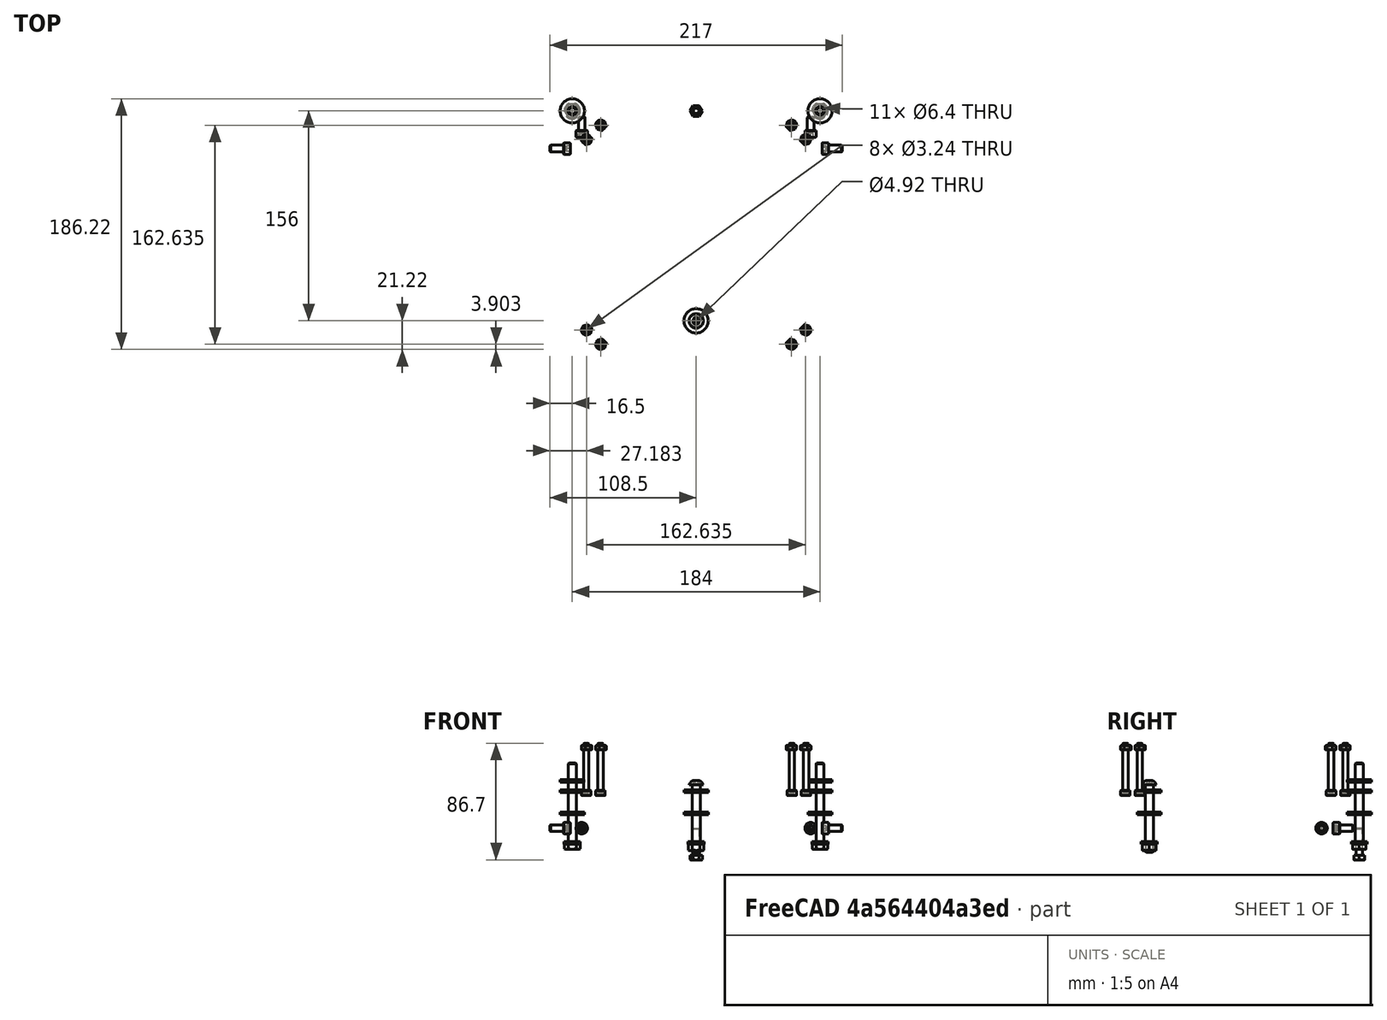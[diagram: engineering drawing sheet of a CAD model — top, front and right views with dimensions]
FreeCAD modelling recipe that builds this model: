
FCSTD DOCUMENT  (FreeCAD 0.19R24276 (Git))
Label: v5.6_Primary
License: All rights reserved
LicenseURL: http://en.wikipedia.org/wiki/All_rights_reserved
objects: App::Link×38, Part::FeaturePython×36, PartDesign::CoordinateSystem×7, App::DocumentObjectGroup×2, App::FeaturePython×1, App::Part×1
note: 43 computed .brp shape members not serialized (recipe doc carries the construction recipe); baked Part::Feature solids carry a one-line shape summary decoded from their .brp
EXTERNAL_REF file=v5.6_Master.FCStd obj=Local_CS
EXTERNAL_REF file=v5.6_Master.FCStd obj=Body014
EXTERNAL_REF file=v5.6_Master.FCStd obj=Local_CS001
EXTERNAL_REF file=v5.6_Master.FCStd obj=Local_CS005
EXTERNAL_REF file=v5.6_Master.FCStd obj=Body
EXTERNAL_REF file=v5.6_Master.FCStd obj=Local_CS002
EXTERNAL_REF file=v5.6_Master.FCStd obj=Local_CS006
EXTERNAL_REF file=v5.6_Master.FCStd obj=Body002
EXTERNAL_REF file=v5.6_Master.FCStd obj=Local_CS007
EXTERNAL_REF file=v5.6_Master.FCStd obj=Local_CS008
EXTERNAL_REF file=v5.6_Master.FCStd obj=LCS_LowerCell_Float_X
EXTERNAL_REF file=v5.6_Master.FCStd obj=Local_CS012
EXTERNAL_REF file=v5.6_Master.FCStd obj=Part
EXTERNAL_REF file=v5.6_Master.FCStd obj=LCS_LowerCell_RockerHole_P
EXTERNAL_REF file=v5.6_Master.FCStd obj=Local_CS024
EXTERNAL_REF file=v5.6_Master.FCStd obj=Body006
EXTERNAL_REF file=v5.6_Master.FCStd obj=LCS_LowerCell_RockerHole_S
EXTERNAL_REF file=v5.6_Master.FCStd obj=Local_CS028
EXTERNAL_REF file=v5.6_Master.FCStd obj=LCS_LowerCell_BCorner_AP
EXTERNAL_REF file=v5.6_Master.FCStd obj=Local_CS097
EXTERNAL_REF file=v5.6_Master.FCStd obj=Body038
EXTERNAL_REF file=v5.6_Master.FCStd obj=LCS_LowerCell_BCorner_AS
EXTERNAL_REF file=v5.6_Master.FCStd obj=LCS_LowerCell_CollPoint_F
EXTERNAL_REF file=v5.6_Master.FCStd obj=Local_CS191
EXTERNAL_REF file=v5.6_Master.FCStd obj=Body022010
EXTERNAL_REF file=v5.6_Master.FCStd obj=LCS_LowerCell_CollPoint_AP
EXTERNAL_REF file=v5.6_Master.FCStd obj=LCS_LowerCell_CollPoint_AS
EXTERNAL_REF file=v5.6_Master.FCStd obj=Local_CS081
EXTERNAL_REF file=v5.6_Master.FCStd obj=Local_CS086
EXTERNAL_REF file=v5.6_Master.FCStd obj=Body022
EXTERNAL_REF file=v5.6_Master.FCStd obj=Local_CS082
EXTERNAL_REF file=v5.6_Master.FCStd obj=Local_CS080
EXTERNAL_REF file=v5.6_Master.FCStd obj=Local_CS083
EXTERNAL_REF file=v5.6_Master.FCStd obj=Local_CS100
EXTERNAL_REF file=v5.6_Master.FCStd obj=Body039
EXTERNAL_REF file=v5.6_Master.FCStd obj=Local_CS026
EXTERNAL_REF file=v5.6_Master.FCStd obj=Local_CS030
EXTERNAL_REF file=v5.6_Master.FCStd obj=Local_CS108
EXTERNAL_REF file=v5.6_Master.FCStd obj=Local_CS109
EXTERNAL_REF file=v5.6_Master.FCStd obj=Local_CS009
EXTERNAL_REF file=v5.6_Master.FCStd obj=Local_CS114
EXTERNAL_REF file=v5.6_Master.FCStd obj=Local_CS115
EXTERNAL_REF file=v5.6_Master.FCStd obj=Local_CS116
EXTERNAL_REF file=v5.6_Master.FCStd obj=Local_CS117
EXTERNAL_REF file=v5.6_Master.FCStd obj=Local_CS118
EXTERNAL_REF file=v5.6_Master.FCStd obj=Local_CS119
EXTERNAL_REF file=v5.6_Master.FCStd obj=Local_CS120
EXTERNAL_REF file=v5.6_Master.FCStd obj=Local_CS121
EXTERNAL_REF file=v5.6_Master.FCStd obj=Local_CS098
EXTERNAL_REF file=v5.6_Master.FCStd obj=Local_CS099
EXTERNAL_REF file=v5.6_Master.FCStd obj=LCS_LowerCell_Pole_AP
EXTERNAL_REF file=v5.6_Master.FCStd obj=LCS_LowerCell_Pole_FP
EXTERNAL_REF file=v5.6_Master.FCStd obj=LCS_LowerCell_Pivot_X
EXTERNAL_REF file=v5.6_Master.FCStd obj=Local_CS039
EXTERNAL_REF file=v5.6_Master.FCStd obj=LCS_LowerCell_Pole_AS
EXTERNAL_REF file=v5.6_Master.FCStd obj=LCS_LowerCell_Pole_FS
EXTERNAL_REF file=v5.6_Master.FCStd obj=Local_CS011
EXTERNAL_REF file=v5.6_Master.FCStd obj=Local_CS010
EXTERNAL_REF file=v5.6_Master.FCStd obj=LCS_LowerCell_Counterweight
EXTERNAL_REF file=v5.6_Master.FCStd obj=Local_CS209
EXTERNAL_REF file=v5.6_Master.FCStd obj=Body022019
EXTERNAL_REF file=v5.6_Master.FCStd obj=Local_CS210
EXTERNAL_REF file=v5.6_Master.FCStd obj=Local_CS211
EXTERNAL_REF file=v5.6_Master.FCStd obj=Local_CS218
EXTERNAL_REF file=v5.6_Master.FCStd obj=Body017
EXTERNAL_REF file=v5.6_Master.FCStd obj=Local_CS087
EXTERNAL_REF file=v5.6_Master.FCStd obj=Local_CS088
EXTERNAL_REF file=v5.6_Master.FCStd obj=Local_CS235
EXTERNAL_REF file=v5.6_Master.FCStd obj=Body022032
EXTERNAL_REF file=v5.6_Master.FCStd obj=Local_CS234
EXTERNAL_REF file=v5.6_Master.FCStd obj=Body022030

FEATURE [App::DocumentObjectGroup] Parts
FEATURE [PartDesign::CoordinateSystem] LCS_Origin
  AttacherType = Attacher::AttachEngine3D
  MapMode = 2
  Support = -> [X_Axis]
FEATURE [App::DocumentObjectGroup] Constraints
FEATURE [App::FeaturePython] Variables  # WARN: FeaturePython — macro-defined, semantics opaque (R4)
FEATURE [App::Link] PrimaryMirror
  AssemblyType = Asm4EE
  AttachedBy = #Local_CS
  AttachedTo = Parent Assembly#LCS_Origin
  LinkedObject = -> <external v5.6_Master.FCStd>#Body014
  expr: Placement = LCS_Origin.Placement * AttachmentOffset * v5_6_Master#Local_CS.Placement ^ -1
FEATURE [App::Link] UpperCell
  AssemblyType = Asm4EE
  AttachedBy = #Local_CS005
  AttachedTo = PrimaryMirror#Local_CS001
  AttachmentOffset = pos=(0,0,0) rot=(0,0,1;1.5708rad)
  LinkPlacement = pos=(0,0,-37) rot=(0,0,1;0rad)
  LinkedObject = -> <external v5.6_Master.FCStd>#Body
  Placement = pos=(0,0,-37) rot=(0,0,1;0rad)
  expr: Placement = PrimaryMirror.Placement * v5_6_Master#Local_CS001.Placement * AttachmentOffset * v5_6_Master#Local_CS005.Placement ^ -1
FEATURE [App::Link] LowerPad_A
  AssemblyType = Asm4EE
  AttachedBy = #Local_CS002
  AttachedTo = UpperCell#Local_CS006
  LinkPlacement = pos=(0,60,-31) rot=(0,0,-1;1.5708rad)
  LinkedObject = -> <external v5.6_Master.FCStd>#Body002
  Placement = pos=(0,60,-31) rot=(0,0,-1;1.5708rad)
  expr: Placement = UpperCell.Placement * v5_6_Master#Local_CS006.Placement * AttachmentOffset * v5_6_Master#Local_CS002.Placement ^ -1
FEATURE [App::Link] LowerPad_FP
  AssemblyType = Asm4EE
  AttachedBy = #Local_CS002
  AttachedTo = UpperCell#Local_CS007
  LinkPlacement = pos=(51.9615,-30,-31) rot=(0,0,-1;3.66519rad)
  LinkedObject = -> <external v5.6_Master.FCStd>#Body002
  Placement = pos=(51.9615,-30,-31) rot=(0,0,-1;3.66519rad)
  expr: Placement = UpperCell.Placement * v5_6_Master#Local_CS007.Placement * AttachmentOffset * v5_6_Master#Local_CS002.Placement ^ -1
FEATURE [App::Link] LowerPad_FS
  AssemblyType = Asm4EE
  AttachedBy = #Local_CS002
  AttachedTo = UpperCell#Local_CS008
  LinkPlacement = pos=(-51.9615,-30,-31) rot=(0,0,1;0.523599rad)
  LinkedObject = -> <external v5.6_Master.FCStd>#Body002
  Placement = pos=(-51.9615,-30,-31) rot=(0,0,1;0.523599rad)
  expr: Placement = UpperCell.Placement * v5_6_Master#Local_CS008.Placement * AttachmentOffset * v5_6_Master#Local_CS002.Placement ^ -1
FEATURE [App::Link] LowerCell
  AssemblyType = Asm4EE
  AttachedBy = #LCS_LowerCell_Float_X
  AttachedTo = UpperCell#Local_CS012
  AttachmentOffset = pos=(0,0,0) rot=(0,0,1;4.71239rad)
  LinkPlacement = pos=(0,0,-65.2) rot=(0,0,1;0rad)
  LinkedObject = -> <external v5.6_Master.FCStd>#Part
  Placement = pos=(0,0,-65.2) rot=(0,0,1;0rad)
  expr: Placement = UpperCell.Placement * v5_6_Master#Local_CS012.Placement * AttachmentOffset * v5_6_Master#LCS_LowerCell_Float_X.Placement ^ -1
FEATURE [App::Link] Rocker_P
  AssemblyType = Asm4EE
  AttachedBy = #Local_CS024
  AttachedTo = LowerCell#LCS_LowerCell_RockerHole_P
  AttachmentOffset = pos=(0,0,0) rot=(0,1,0;3.14159rad)
  LinkPlacement = pos=(128,-7.11e-14,79.8) rot=(0,0,1;0rad)
  LinkedObject = -> <external v5.6_Master.FCStd>#Body006
  Placement = pos=(128,-7.11e-14,79.8) rot=(0,0,1;0rad)
  expr: Placement = LowerCell.Placement * v5_6_Master#LCS_LowerCell_RockerHole_P.Placement * AttachmentOffset * v5_6_Master#Local_CS024.Placement ^ -1
FEATURE [App::Link] Rocker_S
  AssemblyType = Asm4EE
  AttachedBy = #Local_CS028
  AttachedTo = LowerCell#LCS_LowerCell_RockerHole_S
  AttachmentOffset = pos=(0,0,0) rot=(1,0,0;3.14159rad)
  LinkPlacement = pos=(-128,5.68e-14,79.8) rot=(0,0,1;0rad)
  LinkedObject = -> <external v5.6_Master.FCStd>#Body006
  Placement = pos=(-128,5.68e-14,79.8) rot=(0,0,1;0rad)
  expr: Placement = LowerCell.Placement * v5_6_Master#LCS_LowerCell_RockerHole_S.Placement * AttachmentOffset * v5_6_Master#Local_CS028.Placement ^ -1
FEATURE [App::Link] LCFrame_Bracket_AP
  AssemblyType = Asm4EE
  AttachedBy = #Local_CS097
  AttachedTo = LowerCell#LCS_LowerCell_BCorner_AP
  AttachmentOffset = pos=(0,0,0) rot=(0,0,1;3.14159rad)
  LinkPlacement = pos=(103,82,-65.2) rot=(0,0,-1;3.14159rad)
  LinkedObject = -> <external v5.6_Master.FCStd>#Body038
  Placement = pos=(103,82,-65.2) rot=(0,0,-1;3.14159rad)
  expr: Placement = LowerCell.Placement * v5_6_Master#LCS_LowerCell_BCorner_AP.Placement * AttachmentOffset * v5_6_Master#Local_CS097.Placement ^ -1
FEATURE [App::Link] LCFrame_Bracket_AS
  AssemblyType = Asm4EE
  AttachedBy = #Local_CS097
  AttachedTo = LowerCell#LCS_LowerCell_BCorner_AS
  AttachmentOffset = pos=(0,0,0) rot=(0,0,1;4.71239rad)
  LinkPlacement = pos=(-103,82,-65.2) rot=(0,0,-1;1.5708rad)
  LinkedObject = -> <external v5.6_Master.FCStd>#Body038
  Placement = pos=(-103,82,-65.2) rot=(0,0,-1;1.5708rad)
  expr: Placement = LowerCell.Placement * v5_6_Master#LCS_LowerCell_BCorner_AS.Placement * AttachmentOffset * v5_6_Master#Local_CS097.Placement ^ -1
FEATURE [App::Link] CollSpring_F
  AssemblyType = Asm4EE
  AttachedBy = #Local_CS191
  AttachedTo = LowerCell#LCS_LowerCell_CollPoint_F
  AttachmentOffset = pos=(0,0,11.6) rot=(0,0,1;0rad)
  LinkPlacement = pos=(-2.84e-14,-64,-53.6) rot=(0,0,1;0rad)
  LinkedObject = -> <external v5.6_Master.FCStd>#Body022010
  Placement = pos=(-2.84e-14,-64,-53.6) rot=(0,0,1;0rad)
  expr: Placement = LowerCell.Placement * v5_6_Master#LCS_LowerCell_CollPoint_F.Placement * AttachmentOffset * v5_6_Master#Local_CS191.Placement ^ -1
FEATURE [App::Link] CollSpring_AP
  AssemblyType = Asm4EE
  AttachedBy = #Local_CS191
  AttachedTo = LowerCell#LCS_LowerCell_CollPoint_AP
  AttachmentOffset = pos=(0,0,11.6) rot=(0,0,1;0rad)
  LinkPlacement = pos=(92,92,-53.6) rot=(0,0,1;0rad)
  LinkedObject = -> <external v5.6_Master.FCStd>#Body022010
  Placement = pos=(92,92,-53.6) rot=(0,0,1;0rad)
  expr: Placement = LowerCell.Placement * v5_6_Master#LCS_LowerCell_CollPoint_AP.Placement * AttachmentOffset * v5_6_Master#Local_CS191.Placement ^ -1
FEATURE [App::Link] CollSpring_AS
  AssemblyType = Asm4EE
  AttachedBy = #Local_CS191
  AttachedTo = LowerCell#LCS_LowerCell_CollPoint_AS
  AttachmentOffset = pos=(0,0,11.6) rot=(0,0,1;0rad)
  LinkPlacement = pos=(-92,92,-53.6) rot=(0,0,1;0rad)
  LinkedObject = -> <external v5.6_Master.FCStd>#Body022010
  Placement = pos=(-92,92,-53.6) rot=(0,0,1;0rad)
  expr: Placement = LowerCell.Placement * v5_6_Master#LCS_LowerCell_CollPoint_AS.Placement * AttachmentOffset * v5_6_Master#Local_CS191.Placement ^ -1
FEATURE [App::Link] MirrorClip_AP
  AssemblyType = Asm4EE
  AttachedBy = #Local_CS086
  AttachedTo = UpperCell#Local_CS081
  LinkPlacement = pos=(72.4784,72.4784,-31) rot=(0,0,-1;0.785398rad)
  LinkedObject = -> <external v5.6_Master.FCStd>#Body022
  Placement = pos=(72.4784,72.4784,-31) rot=(0,0,-1;0.785398rad)
  expr: Placement = UpperCell.Placement * v5_6_Master#Local_CS081.Placement * AttachmentOffset * v5_6_Master#Local_CS086.Placement ^ -1
FEATURE [App::Link] MirrorClip_FP
  AssemblyType = Asm4EE
  AttachedBy = #Local_CS086
  AttachedTo = UpperCell#Local_CS082
  LinkPlacement = pos=(72.4784,-72.4784,-31) rot=(0,0,-1;2.35619rad)
  LinkedObject = -> <external v5.6_Master.FCStd>#Body022
  Placement = pos=(72.4784,-72.4784,-31) rot=(0,0,-1;2.35619rad)
  expr: Placement = UpperCell.Placement * v5_6_Master#Local_CS082.Placement * AttachmentOffset * v5_6_Master#Local_CS086.Placement ^ -1
FEATURE [App::Link] MirrorClip_AS
  AssemblyType = Asm4EE
  AttachedBy = #Local_CS086
  AttachedTo = UpperCell#Local_CS080
  LinkPlacement = pos=(-72.4784,72.4784,-31) rot=(0,0,-1;5.49779rad)
  LinkedObject = -> <external v5.6_Master.FCStd>#Body022
  Placement = pos=(-72.4784,72.4784,-31) rot=(0,0,-1;5.49779rad)
  expr: Placement = UpperCell.Placement * v5_6_Master#Local_CS080.Placement * AttachmentOffset * v5_6_Master#Local_CS086.Placement ^ -1
FEATURE [App::Link] MirrorClip_FS
  AssemblyType = Asm4EE
  AttachedBy = #Local_CS086
  AttachedTo = UpperCell#Local_CS083
  LinkPlacement = pos=(-72.4784,-72.4784,-31) rot=(0,0,-1;3.92699rad)
  LinkedObject = -> <external v5.6_Master.FCStd>#Body022
  Placement = pos=(-72.4784,-72.4784,-31) rot=(0,0,-1;3.92699rad)
  expr: Placement = UpperCell.Placement * v5_6_Master#Local_CS083.Placement * AttachmentOffset * v5_6_Master#Local_CS086.Placement ^ -1
FEATURE [App::Link] Rocker_P_TNut_A
  AssemblyType = Asm4EE
  AttachedBy = #Local_CS100
  AttachedTo = Rocker_P#Local_CS024
  AttachmentOffset = pos=(0,0,0) rot=(0.707107,-0.707107,0;3.14159rad)
  LinkPlacement = pos=(121.8,113,-65.2) rot=(-0.57735,0.57735,-0.57735;2.0944rad)
  LinkedObject = -> <external v5.6_Master.FCStd>#Body039
  Placement = pos=(121.8,113,-65.2) rot=(-0.57735,0.57735,-0.57735;2.0944rad)
  expr: Placement = Rocker_P.Placement * v5_6_Master#Local_CS024.Placement * AttachmentOffset * v5_6_Master#Local_CS100.Placement ^ -1
FEATURE [App::Link] Rocker_P_TNut_F
  AssemblyType = Asm4EE
  AttachedBy = #Local_CS100
  AttachedTo = Rocker_P#Local_CS026
  AttachmentOffset = pos=(0,0,0) rot=(0.707107,-0.707107,0;3.14159rad)
  LinkPlacement = pos=(121.8,-113,-65.2) rot=(-0.57735,0.57735,-0.57735;2.0944rad)
  LinkedObject = -> <external v5.6_Master.FCStd>#Body039
  Placement = pos=(121.8,-113,-65.2) rot=(-0.57735,0.57735,-0.57735;2.0944rad)
  expr: Placement = Rocker_P.Placement * v5_6_Master#Local_CS026.Placement * AttachmentOffset * v5_6_Master#Local_CS100.Placement ^ -1
FEATURE [App::Link] Rocker_S_TNut_A
  AssemblyType = Asm4EE
  AttachedBy = #Local_CS100
  AttachedTo = Rocker_S#Local_CS028
  AttachmentOffset = pos=(0,0,0) rot=(0.707107,-0.707107,0;3.14159rad)
  LinkPlacement = pos=(-121.8,113,-65.2) rot=(0.57735,-0.57735,-0.57735;2.0944rad)
  LinkedObject = -> <external v5.6_Master.FCStd>#Body039
  Placement = pos=(-121.8,113,-65.2) rot=(0.57735,-0.57735,-0.57735;2.0944rad)
  expr: Placement = Rocker_S.Placement * v5_6_Master#Local_CS028.Placement * AttachmentOffset * v5_6_Master#Local_CS100.Placement ^ -1
FEATURE [App::Link] Rocker_S_TNut_F
  AssemblyType = Asm4EE
  AttachedBy = #Local_CS100
  AttachedTo = Rocker_S#Local_CS030
  AttachmentOffset = pos=(0,0,0) rot=(0.707107,-0.707107,0;3.14159rad)
  LinkPlacement = pos=(-121.8,-113,-65.2) rot=(0.57735,-0.57735,-0.57735;2.0944rad)
  LinkedObject = -> <external v5.6_Master.FCStd>#Body039
  Placement = pos=(-121.8,-113,-65.2) rot=(0.57735,-0.57735,-0.57735;2.0944rad)
  expr: Placement = Rocker_S.Placement * v5_6_Master#Local_CS030.Placement * AttachmentOffset * v5_6_Master#Local_CS100.Placement ^ -1
FEATURE [App::Link] LCBracket_AP_TNut_P
  AssemblyType = Asm4EE
  AttachedBy = #Local_CS100
  AttachedTo = LCFrame_Bracket_AP#Local_CS108
  LinkPlacement = pos=(104.2,64,-65.2) rot=(0.57735,0.57735,-0.57735;4.18879rad)
  LinkedObject = -> <external v5.6_Master.FCStd>#Body039
  Placement = pos=(104.2,64,-65.2) rot=(0.57735,0.57735,-0.57735;4.18879rad)
  expr: Placement = LCFrame_Bracket_AP.Placement * v5_6_Master#Local_CS108.Placement * AttachmentOffset * v5_6_Master#Local_CS100.Placement ^ -1
FEATURE [App::Link] LCBracket_AP_TNut_A
  AssemblyType = Asm4EE
  AttachedBy = #Local_CS100
  AttachedTo = LCFrame_Bracket_AP#Local_CS109
  LinkPlacement = pos=(85,83.2,-65.2) rot=(0,0.707107,-0.707107;3.14159rad)
  LinkedObject = -> <external v5.6_Master.FCStd>#Body039
  Placement = pos=(85,83.2,-65.2) rot=(0,0.707107,-0.707107;3.14159rad)
  expr: Placement = LCFrame_Bracket_AP.Placement * v5_6_Master#Local_CS109.Placement * AttachmentOffset * v5_6_Master#Local_CS100.Placement ^ -1
FEATURE [App::Link] LCBracket_AS_TNut_S
  AssemblyType = Asm4EE
  AttachedBy = #Local_CS100
  AttachedTo = LCFrame_Bracket_AS#Local_CS109
  LinkPlacement = pos=(-104.2,64,-65.2) rot=(-0.57735,0.57735,-0.57735;2.0944rad)
  LinkedObject = -> <external v5.6_Master.FCStd>#Body039
  Placement = pos=(-104.2,64,-65.2) rot=(-0.57735,0.57735,-0.57735;2.0944rad)
  expr: Placement = LCFrame_Bracket_AS.Placement * v5_6_Master#Local_CS109.Placement * AttachmentOffset * v5_6_Master#Local_CS100.Placement ^ -1
FEATURE [App::Link] LCBracket_AS_TNut_A
  AssemblyType = Asm4EE
  AttachedBy = #Local_CS100
  AttachedTo = LCFrame_Bracket_AS#Local_CS108
  LinkPlacement = pos=(-85,83.2,-65.2) rot=(0,0.707107,-0.707107;3.14159rad)
  LinkedObject = -> <external v5.6_Master.FCStd>#Body039
  Placement = pos=(-85,83.2,-65.2) rot=(0,0.707107,-0.707107;3.14159rad)
  expr: Placement = LCFrame_Bracket_AS.Placement * v5_6_Master#Local_CS108.Placement * AttachmentOffset * v5_6_Master#Local_CS100.Placement ^ -1
FEATURE [Part::FeaturePython] Screw  label="M6x50-Screw"  # Fasteners workbench fastener (typed FeaturePython)
  AssemblyType = Asm4EE
  AttachedBy = Origin
  AttachedTo = UpperCell#Local_CS009
  Placement = pos=(0,-64,-33) rot=(0,0,1;0rad)
  diameter = 4
  invert = false
  length = 10
  lengthCustom = 50
  matchOuter = false
  offset = 0
  thread = false
  type = 38
  expr: Placement = UpperCell.Placement * v5_6_Master#Local_CS009.Placement * AttachmentOffset
FEATURE [Part::FeaturePython] Screw001  label="M6x60-Screw"  # Fasteners workbench fastener (typed FeaturePython)
  AssemblyType = Asm4EE
  AttachedBy = Origin
  AttachedTo = LowerCell#LCS_LowerCell_CollPoint_AP
  AttachmentOffset = pos=(0,0,-11.6) rot=(1,0,0;3.14159rad)
  Placement = pos=(92,92,-76.8) rot=(-1,0,0;3.14159rad)
  diameter = 8
  invert = false
  length = 11
  lengthCustom = 60
  matchOuter = false
  offset = 0
  thread = false
  type = 27
  expr: Placement = LowerCell.Placement * v5_6_Master#LCS_LowerCell_CollPoint_AP.Placement * AttachmentOffset
FEATURE [Part::FeaturePython] Screw002  label="M6x60-Screw001"  # Fasteners workbench fastener (typed FeaturePython)
  AssemblyType = Asm4EE
  AttachedBy = Origin
  AttachedTo = LowerCell#LCS_LowerCell_CollPoint_AS
  AttachmentOffset = pos=(0,0,-11.6) rot=(1,0,0;3.14159rad)
  Placement = pos=(-92,92,-76.8) rot=(-1,0,0;3.14159rad)
  diameter = 8
  invert = false
  length = 11
  lengthCustom = 60
  matchOuter = false
  offset = 0
  thread = false
  type = 27
  expr: Placement = LowerCell.Placement * v5_6_Master#LCS_LowerCell_CollPoint_AS.Placement * AttachmentOffset
FEATURE [Part::FeaturePython] Washer  label="M6-Washer"  # Fasteners workbench fastener (typed FeaturePython)
  AssemblyType = Asm4EE
  AttachedBy = Origin
  AttachedTo = LowerCell#LCS_LowerCell_CollPoint_F
  AttachmentOffset = pos=(0,0,10) rot=(0,0,1;0rad)
  Placement = pos=(-2.84e-14,-64,-55.2) rot=(0,0,1;0rad)
  diameter = 5
  invert = false
  matchOuter = false
  offset = 0
  type = 6
  expr: Placement = LowerCell.Placement * v5_6_Master#LCS_LowerCell_CollPoint_F.Placement * AttachmentOffset
FEATURE [Part::FeaturePython] Washer001  label="M6-Washer413"  # Fasteners workbench fastener (typed FeaturePython)
  AssemblyType = Asm4EE
  AttachedBy = Origin
  AttachedTo = LowerCell#LCS_LowerCell_CollPoint_F
  AttachmentOffset = pos=(0,0,26.6) rot=(0,0,1;0rad)
  Placement = pos=(-2.84e-14,-64,-38.6) rot=(0,0,1;0rad)
  diameter = 5
  invert = false
  matchOuter = false
  offset = 0
  type = 6
  expr: Placement = LowerCell.Placement * v5_6_Master#LCS_LowerCell_CollPoint_F.Placement * AttachmentOffset
FEATURE [Part::FeaturePython] Washer002  label="M6-Washer414"  # Fasteners workbench fastener (typed FeaturePython)
  AssemblyType = Asm4EE
  AttachedBy = Origin
  AttachedTo = LowerCell#LCS_LowerCell_CollPoint_AP
  AttachmentOffset = pos=(0,0,10) rot=(0,0,1;0rad)
  Placement = pos=(92,92,-55.2) rot=(0,0,1;0rad)
  diameter = 5
  invert = false
  matchOuter = false
  offset = 0
  type = 6
  expr: Placement = LowerCell.Placement * v5_6_Master#LCS_LowerCell_CollPoint_AP.Placement * AttachmentOffset
FEATURE [Part::FeaturePython] Washer003  label="M6-Washer415"  # Fasteners workbench fastener (typed FeaturePython)
  AssemblyType = Asm4EE
  AttachedBy = Origin
  AttachedTo = LowerCell#LCS_LowerCell_CollPoint_AP
  AttachmentOffset = pos=(0,0,26.6) rot=(0,0,1;0rad)
  Placement = pos=(92,92,-38.6) rot=(0,0,1;0rad)
  diameter = 5
  invert = false
  matchOuter = false
  offset = 0
  type = 6
  expr: Placement = LowerCell.Placement * v5_6_Master#LCS_LowerCell_CollPoint_AP.Placement * AttachmentOffset
FEATURE [Part::FeaturePython] Washer004  label="M6-Washer416"  # Fasteners workbench fastener (typed FeaturePython)
  AssemblyType = Asm4EE
  AttachedBy = Origin
  AttachedTo = LowerCell#LCS_LowerCell_CollPoint_AS
  AttachmentOffset = pos=(0,0,10) rot=(0,0,1;0rad)
  Placement = pos=(-92,92,-55.2) rot=(0,0,1;0rad)
  diameter = 5
  invert = false
  matchOuter = false
  offset = 0
  type = 6
  expr: Placement = LowerCell.Placement * v5_6_Master#LCS_LowerCell_CollPoint_AS.Placement * AttachmentOffset
FEATURE [Part::FeaturePython] Washer005  label="M6-Washer417"  # Fasteners workbench fastener (typed FeaturePython)
  AssemblyType = Asm4EE
  AttachedBy = Origin
  AttachedTo = LowerCell#LCS_LowerCell_CollPoint_AS
  AttachmentOffset = pos=(0,0,26.6) rot=(0,0,1;0rad)
  Placement = pos=(-92,92,-38.6) rot=(0,0,1;0rad)
  diameter = 5
  invert = false
  matchOuter = false
  offset = 0
  type = 6
  expr: Placement = LowerCell.Placement * v5_6_Master#LCS_LowerCell_CollPoint_AS.Placement * AttachmentOffset
FEATURE [Part::FeaturePython] Screw003  label="M4x35-Screw"  # Fasteners workbench fastener (typed FeaturePython)
  AssemblyType = Asm4EE
  AttachedBy = Origin
  AttachedTo = UpperCell#Local_CS114
  Placement = pos=(-81.6708,-71.0642,-37) rot=(0.382683,0.92388,0;3.14159rad)
  diameter = 5
  invert = false
  length = 9
  lengthCustom = 35
  matchOuter = false
  offset = 0
  thread = false
  type = 32
  expr: Placement = UpperCell.Placement * v5_6_Master#Local_CS114.Placement * AttachmentOffset
FEATURE [Part::FeaturePython] Screw004  label="M4x35-Screw211"  # Fasteners workbench fastener (typed FeaturePython)
  AssemblyType = Asm4EE
  AttachedBy = Origin
  AttachedTo = UpperCell#Local_CS115
  Placement = pos=(-71.0642,-81.6708,-37) rot=(0.382683,0.92388,0;3.14159rad)
  diameter = 5
  invert = false
  length = 9
  lengthCustom = 35
  matchOuter = false
  offset = 0
  thread = false
  type = 32
  expr: Placement = UpperCell.Placement * v5_6_Master#Local_CS115.Placement * AttachmentOffset
FEATURE [Part::FeaturePython] Screw005  label="M4x35-Screw212"  # Fasteners workbench fastener (typed FeaturePython)
  AssemblyType = Asm4EE
  AttachedBy = Origin
  AttachedTo = UpperCell#Local_CS116
  Placement = pos=(71.0642,-81.6708,-37) rot=(-0.382683,0.92388,0;3.14159rad)
  diameter = 5
  invert = false
  length = 9
  lengthCustom = 35
  matchOuter = false
  offset = 0
  thread = false
  type = 32
  expr: Placement = UpperCell.Placement * v5_6_Master#Local_CS116.Placement * AttachmentOffset
FEATURE [Part::FeaturePython] Screw006  label="M4x35-Screw213"  # Fasteners workbench fastener (typed FeaturePython)
  AssemblyType = Asm4EE
  AttachedBy = Origin
  AttachedTo = UpperCell#Local_CS117
  Placement = pos=(81.6708,-71.0642,-37) rot=(-0.382683,0.92388,0;3.14159rad)
  diameter = 5
  invert = false
  length = 9
  lengthCustom = 35
  matchOuter = false
  offset = 0
  thread = false
  type = 32
  expr: Placement = UpperCell.Placement * v5_6_Master#Local_CS117.Placement * AttachmentOffset
FEATURE [Part::FeaturePython] Screw007  label="M4x35-Screw214"  # Fasteners workbench fastener (typed FeaturePython)
  AssemblyType = Asm4EE
  AttachedBy = Origin
  AttachedTo = UpperCell#Local_CS118
  Placement = pos=(-81.6708,71.0642,-37) rot=(0.92388,0.382683,0;3.14159rad)
  diameter = 5
  invert = false
  length = 9
  lengthCustom = 35
  matchOuter = false
  offset = 0
  thread = false
  type = 32
  expr: Placement = UpperCell.Placement * v5_6_Master#Local_CS118.Placement * AttachmentOffset
FEATURE [Part::FeaturePython] Screw008  label="M4x35-Screw215"  # Fasteners workbench fastener (typed FeaturePython)
  AssemblyType = Asm4EE
  AttachedBy = Origin
  AttachedTo = UpperCell#Local_CS119
  Placement = pos=(-71.0642,81.6708,-37) rot=(0.92388,0.382683,0;3.14159rad)
  diameter = 5
  invert = false
  length = 9
  lengthCustom = 35
  matchOuter = false
  offset = 0
  thread = false
  type = 32
  expr: Placement = UpperCell.Placement * v5_6_Master#Local_CS119.Placement * AttachmentOffset
FEATURE [Part::FeaturePython] Screw009  label="M4x35-Screw216"  # Fasteners workbench fastener (typed FeaturePython)
  AssemblyType = Asm4EE
  AttachedBy = Origin
  AttachedTo = UpperCell#Local_CS120
  Placement = pos=(81.6708,71.0642,-37) rot=(0.92388,-0.382683,0;3.14159rad)
  diameter = 5
  invert = false
  length = 9
  lengthCustom = 35
  matchOuter = false
  offset = 0
  thread = false
  type = 32
  expr: Placement = UpperCell.Placement * v5_6_Master#Local_CS120.Placement * AttachmentOffset
FEATURE [Part::FeaturePython] Screw010  label="M4x35-Screw217"  # Fasteners workbench fastener (typed FeaturePython)
  AssemblyType = Asm4EE
  AttachedBy = Origin
  AttachedTo = UpperCell#Local_CS121
  Placement = pos=(71.0642,81.6708,-37) rot=(0.92388,-0.382683,0;3.14159rad)
  diameter = 5
  invert = false
  length = 9
  lengthCustom = 35
  matchOuter = false
  offset = 0
  thread = false
  type = 32
  expr: Placement = UpperCell.Placement * v5_6_Master#Local_CS121.Placement * AttachmentOffset
FEATURE [Part::FeaturePython] Screw011  label="M5x10-Screw"  # Fasteners workbench fastener (typed FeaturePython)
  AssemblyType = Asm4EE
  AttachedBy = Origin
  AttachedTo = LCFrame_Bracket_AP#Local_CS098
  Placement = pos=(98.5,64,-65.2) rot=(0.57735,-0.57735,-0.57735;2.0944rad)
  diameter = 6
  invert = false
  length = 1
  lengthCustom = 10
  matchOuter = false
  offset = 0
  thread = false
  type = 32
  expr: Placement = LCFrame_Bracket_AP.Placement * v5_6_Master#Local_CS098.Placement * AttachmentOffset
FEATURE [Part::FeaturePython] Screw012  label="M5x10-Screw133"  # Fasteners workbench fastener (typed FeaturePython)
  AssemblyType = Asm4EE
  AttachedBy = Origin
  AttachedTo = LCFrame_Bracket_AP#Local_CS099
  Placement = pos=(85,77.5,-65.2) rot=(0.57735,0.57735,-0.57735;2.0944rad)
  diameter = 6
  invert = false
  length = 1
  lengthCustom = 10
  matchOuter = false
  offset = 0
  thread = false
  type = 32
  expr: Placement = LCFrame_Bracket_AP.Placement * v5_6_Master#Local_CS099.Placement * AttachmentOffset
FEATURE [Part::FeaturePython] Screw013  label="M5x10-Screw134"  # Fasteners workbench fastener (typed FeaturePython)
  AssemblyType = Asm4EE
  AttachedBy = Origin
  AttachedTo = LCFrame_Bracket_AS#Local_CS098
  Placement = pos=(-85,77.5,-65.2) rot=(1,0,0;1.5708rad)
  diameter = 6
  invert = false
  length = 1
  lengthCustom = 10
  matchOuter = false
  offset = 0
  thread = false
  type = 32
  expr: Placement = LCFrame_Bracket_AS.Placement * v5_6_Master#Local_CS098.Placement * AttachmentOffset
FEATURE [Part::FeaturePython] Screw014  label="M5x10-Screw135"  # Fasteners workbench fastener (typed FeaturePython)
  AssemblyType = Asm4EE
  AttachedBy = Origin
  AttachedTo = LCFrame_Bracket_AS#Local_CS099
  Placement = pos=(-98.5,64,-65.2) rot=(0,1,0;1.5708rad)
  diameter = 6
  invert = false
  length = 1
  lengthCustom = 10
  matchOuter = false
  offset = 0
  thread = false
  type = 32
  expr: Placement = LCFrame_Bracket_AS.Placement * v5_6_Master#Local_CS099.Placement * AttachmentOffset
FEATURE [App::Link] PoleBase_TNut_A
  AssemblyType = Asm4EE
  AttachedBy = #Local_CS100
  AttachedTo = LowerCell#LCS_LowerCell_Pole_AP
  AttachmentOffset = pos=(0,0,0) rot=(0,0,1;1.5708rad)
  LinkPlacement = pos=(113,113,-56.4) rot=(0,0,1;4.71239rad)
  LinkedObject = -> <external v5.6_Master.FCStd>#Body039
  Placement = pos=(113,113,-56.4) rot=(0,0,1;4.71239rad)
  expr: Placement = LowerCell.Placement * v5_6_Master#LCS_LowerCell_Pole_AP.Placement * AttachmentOffset * v5_6_Master#Local_CS100.Placement ^ -1
FEATURE [App::Link] PoleBase_TNut_F
  AssemblyType = Asm4EE
  AttachedBy = #Local_CS100
  AttachedTo = LowerCell#LCS_LowerCell_Pole_FP
  AttachmentOffset = pos=(0,0,0) rot=(0,0,1;1.5708rad)
  LinkPlacement = pos=(113,-113,-56.4) rot=(0,0,1;4.71239rad)
  LinkedObject = -> <external v5.6_Master.FCStd>#Body039
  Placement = pos=(113,-113,-56.4) rot=(0,0,1;4.71239rad)
  expr: Placement = LowerCell.Placement * v5_6_Master#LCS_LowerCell_Pole_FP.Placement * AttachmentOffset * v5_6_Master#Local_CS100.Placement ^ -1
FEATURE [PartDesign::CoordinateSystem] LCS_Pivot
  AttacherType = Attacher::AttachEngine3D
  Placement = pos=(0,0,79.8) rot=(0,0,1;0rad)
  expr: Placement = LowerCell.Placement * v5_6_Master#LCS_LowerCell_Pivot_X.Placement * AttachmentOffset
FEATURE [PartDesign::CoordinateSystem] LCS_SecondaryAssembly
  AttacherType = Attacher::AttachEngine3D
  Placement = pos=(0,0,834) rot=(0,0,1;0rad)
  expr: Placement = PrimaryMirror.Placement * v5_6_Master#Local_CS039.Placement * AttachmentOffset
FEATURE [PartDesign::CoordinateSystem] LCS_Primary_Pole_AP
  AttacherType = Attacher::AttachEngine3D
  Placement = pos=(113,113,-55.2) rot=(0,0,1;0rad)
  expr: Placement = LowerCell.Placement * v5_6_Master#LCS_LowerCell_Pole_AP.Placement * AttachmentOffset
FEATURE [PartDesign::CoordinateSystem] LCS_Primary_Pole_AS
  AttacherType = Attacher::AttachEngine3D
  Placement = pos=(-113,113,-65.2) rot=(0,0,1;0rad)
  expr: Placement = LowerCell.Placement * v5_6_Master#LCS_LowerCell_Pole_AS.Placement * AttachmentOffset
FEATURE [PartDesign::CoordinateSystem] LCS_Primary_Pole_FP
  AttacherType = Attacher::AttachEngine3D
  Placement = pos=(113,-113,-55.2) rot=(0,0,1;0rad)
  expr: Placement = LowerCell.Placement * v5_6_Master#LCS_LowerCell_Pole_FP.Placement * AttachmentOffset
FEATURE [PartDesign::CoordinateSystem] LCS_Primary_Pole_FS
  AttacherType = Attacher::AttachEngine3D
  Placement = pos=(-113,-113,-55.2) rot=(0,0,1;0rad)
  expr: Placement = LowerCell.Placement * v5_6_Master#LCS_LowerCell_Pole_FS.Placement * AttachmentOffset
FEATURE [Part::FeaturePython] Washer006  label="M6-Washer418"  # Fasteners workbench fastener (typed FeaturePython)
  AssemblyType = Asm4EE
  AttachedBy = Origin
  AttachedTo = LowerCell#LCS_LowerCell_CollPoint_F
  AttachmentOffset = pos=(0,0,-10) rot=(1,0,0;3.14159rad)
  Placement = pos=(-2.84e-14,-64,-75.2) rot=(-1,0,0;3.14159rad)
  diameter = 7
  invert = false
  matchOuter = false
  offset = 0
  type = 3
  expr: Placement = LowerCell.Placement * v5_6_Master#LCS_LowerCell_CollPoint_F.Placement * AttachmentOffset
FEATURE [Part::FeaturePython] Nut  label="M6-Nut"  # Fasteners workbench fastener (typed FeaturePython)
  AssemblyType = Asm4EE
  AttachedBy = Origin
  AttachedTo = LowerCell#LCS_LowerCell_CollPoint_F
  AttachmentOffset = pos=(0,0,-11.8) rot=(1,0,0;3.14159rad)
  Placement = pos=(-2.84e-14,-64,-77) rot=(-1,0,0;3.14159rad)
  diameter = 8
  invert = false
  matchOuter = false
  offset = 0
  thread = false
  type = 7
  expr: Placement = LowerCell.Placement * v5_6_Master#LCS_LowerCell_CollPoint_F.Placement * AttachmentOffset
FEATURE [Part::FeaturePython] Washer007  label="M6-Washer419"  # Fasteners workbench fastener (typed FeaturePython)
  AssemblyType = Asm4EE
  AttachedBy = Origin
  AttachedTo = UpperCell#Local_CS011
  Placement = pos=(92,92,-31) rot=(0,0,1;0rad)
  diameter = 5
  invert = false
  matchOuter = false
  offset = 0
  type = 6
  expr: Placement = UpperCell.Placement * v5_6_Master#Local_CS011.Placement * AttachmentOffset
FEATURE [Part::FeaturePython] Washer008  label="M6-Washer420"  # Fasteners workbench fastener (typed FeaturePython)
  AssemblyType = Asm4EE
  AttachedBy = Origin
  AttachedTo = UpperCell#Local_CS010
  Placement = pos=(-92,92,-31) rot=(0,0,1;0rad)
  diameter = 5
  invert = false
  matchOuter = false
  offset = 0
  type = 6
  expr: Placement = UpperCell.Placement * v5_6_Master#Local_CS010.Placement * AttachmentOffset
FEATURE [Part::FeaturePython] Washer009  label="M6-Washer421"  # Fasteners workbench fastener (typed FeaturePython)
  AssemblyType = Asm4EE
  AttachedBy = Origin
  AttachedTo = LowerCell#LCS_LowerCell_CollPoint_AP
  AttachmentOffset = pos=(0,0,-10) rot=(1,0,0;3.14159rad)
  Placement = pos=(92,92,-75.2) rot=(-1,0,0;3.14159rad)
  diameter = 7
  invert = false
  matchOuter = false
  offset = 0
  type = 3
  expr: Placement = LowerCell.Placement * v5_6_Master#LCS_LowerCell_CollPoint_AP.Placement * AttachmentOffset
FEATURE [Part::FeaturePython] Washer010  label="M6-Washer422"  # Fasteners workbench fastener (typed FeaturePython)
  AssemblyType = Asm4EE
  AttachedBy = Origin
  AttachedTo = LowerCell#LCS_LowerCell_CollPoint_AS
  AttachmentOffset = pos=(0,0,-10) rot=(1,0,0;3.14159rad)
  Placement = pos=(-92,92,-75.2) rot=(-1,0,0;3.14159rad)
  diameter = 7
  invert = false
  matchOuter = false
  offset = 0
  type = 3
  expr: Placement = LowerCell.Placement * v5_6_Master#LCS_LowerCell_CollPoint_AS.Placement * AttachmentOffset
FEATURE [App::Link] CounterWeightClamp
  AssemblyType = Asm4EE
  AttachedBy = #Local_CS209
  AttachedTo = LowerCell#LCS_LowerCell_Counterweight
  AttachmentOffset = pos=(0,0,0) rot=(1,0,0;3.14159rad)
  LinkPlacement = pos=(4.09e-14,92,-75.2) rot=(0,0,1;0rad)
  LinkedObject = -> <external v5.6_Master.FCStd>#Body022019
  Placement = pos=(4.09e-14,92,-75.2) rot=(0,0,1;0rad)
  expr: Placement = LowerCell.Placement * v5_6_Master#LCS_LowerCell_Counterweight.Placement * AttachmentOffset * v5_6_Master#Local_CS209.Placement ^ -1
FEATURE [App::Link] CW_TNut
  AssemblyType = Asm4EE
  AttachedBy = #Local_CS100
  AttachedTo = CounterWeightClamp#Local_CS209
  LinkPlacement = pos=(4.09e-14,92,-74) rot=(0,-1,0;3.14159rad)
  LinkedObject = -> <external v5.6_Master.FCStd>#Body039
  Placement = pos=(4.09e-14,92,-74) rot=(0,-1,0;3.14159rad)
  expr: Placement = CounterWeightClamp.Placement * v5_6_Master#Local_CS209.Placement * AttachmentOffset * v5_6_Master#Local_CS100.Placement ^ -1
FEATURE [Part::FeaturePython] Screw026  label="M5x20-Screw"  # Fasteners workbench fastener (typed FeaturePython)
  AssemblyType = Asm4EE
  AttachedBy = Origin
  AttachedTo = CounterWeightClamp#Local_CS210
  AttachmentOffset = pos=(0,0,0) rot=(1,0,0;3.14159rad)
  Placement = pos=(4.75e-14,92,-85.2) rot=(0,-1,0;3.14159rad)
  diameter = 7
  invert = false
  length = 5
  lengthCustom = 20
  matchOuter = false
  offset = 0
  thread = false
  type = 27
  expr: Placement = CounterWeightClamp.Placement * v5_6_Master#Local_CS210.Placement * AttachmentOffset
FEATURE [App::Link] CounterWeight
  AssemblyType = Asm4EE
  AttachedBy = #Local_CS218
  AttachedTo = CounterWeightClamp#Local_CS211
  LinkPlacement = pos=(4.09e-14,92,-95.2) rot=(0,0,-1;4.71239rad)
  LinkedObject = -> <external v5.6_Master.FCStd>#Body017
  Placement = pos=(4.09e-14,92,-95.2) rot=(0,0,-1;4.71239rad)
  expr: Placement = CounterWeightClamp.Placement * v5_6_Master#Local_CS211.Placement * AttachmentOffset * v5_6_Master#Local_CS218.Placement ^ -1
FEATURE [Part::FeaturePython] Nut001  label="M4-Nut"  # Fasteners workbench fastener (typed FeaturePython)
  AssemblyType = Asm4EE
  AttachedBy = Origin
  AttachedTo = MirrorClip_AP#Local_CS087
  AttachmentOffset = pos=(0,0,24) rot=(0,0,1;1.5708rad)
  Placement = pos=(81.3173,70.7107,-7) rot=(0,0,1;2.35619rad)
  diameter = 6
  invert = false
  matchOuter = false
  offset = 0
  thread = false
  type = 7
  expr: Placement = MirrorClip_AP.Placement * v5_6_Master#Local_CS087.Placement * AttachmentOffset
FEATURE [Part::FeaturePython] Nut002  label="M4-Nut079"  # Fasteners workbench fastener (typed FeaturePython)
  AssemblyType = Asm4EE
  AttachedBy = Origin
  AttachedTo = MirrorClip_AP#Local_CS088
  AttachmentOffset = pos=(0,0,24) rot=(0,0,1;1.5708rad)
  Placement = pos=(70.7107,81.3173,-7) rot=(0,0,1;2.35619rad)
  diameter = 6
  invert = false
  matchOuter = false
  offset = 0
  thread = false
  type = 7
  expr: Placement = MirrorClip_AP.Placement * v5_6_Master#Local_CS088.Placement * AttachmentOffset
FEATURE [Part::FeaturePython] Nut003  label="M4-Nut080"  # Fasteners workbench fastener (typed FeaturePython)
  AssemblyType = Asm4EE
  AttachedBy = Origin
  AttachedTo = MirrorClip_FP#Local_CS087
  AttachmentOffset = pos=(0,0,24) rot=(0,0,1;1.5708rad)
  Placement = pos=(70.7107,-81.3173,-7) rot=(0,0,1;0.785398rad)
  diameter = 6
  invert = false
  matchOuter = false
  offset = 0
  thread = false
  type = 7
  expr: Placement = MirrorClip_FP.Placement * v5_6_Master#Local_CS087.Placement * AttachmentOffset
FEATURE [Part::FeaturePython] Nut004  label="M4-Nut081"  # Fasteners workbench fastener (typed FeaturePython)
  AssemblyType = Asm4EE
  AttachedBy = Origin
  AttachedTo = MirrorClip_FP#Local_CS088
  AttachmentOffset = pos=(0,0,24) rot=(0,0,1;1.5708rad)
  Placement = pos=(81.3173,-70.7107,-7) rot=(0,0,1;0.785398rad)
  diameter = 6
  invert = false
  matchOuter = false
  offset = 0
  thread = false
  type = 7
  expr: Placement = MirrorClip_FP.Placement * v5_6_Master#Local_CS088.Placement * AttachmentOffset
FEATURE [Part::FeaturePython] Nut005  label="M4-Nut082"  # Fasteners workbench fastener (typed FeaturePython)
  AssemblyType = Asm4EE
  AttachedBy = Origin
  AttachedTo = MirrorClip_AS#Local_CS087
  AttachmentOffset = pos=(0,0,24) rot=(0,0,1;1.5708rad)
  Placement = pos=(-70.7107,81.3173,-7) rot=(0,0,-1;2.35619rad)
  diameter = 6
  invert = false
  matchOuter = false
  offset = 0
  thread = false
  type = 7
  expr: Placement = MirrorClip_AS.Placement * v5_6_Master#Local_CS087.Placement * AttachmentOffset
FEATURE [Part::FeaturePython] Nut006  label="M4-Nut083"  # Fasteners workbench fastener (typed FeaturePython)
  AssemblyType = Asm4EE
  AttachedBy = Origin
  AttachedTo = MirrorClip_AS#Local_CS088
  AttachmentOffset = pos=(0,0,24) rot=(0,0,1;0rad)
  Placement = pos=(-81.3173,70.7107,-7) rot=(0,0,-1;3.92699rad)
  diameter = 6
  invert = false
  matchOuter = false
  offset = 0
  thread = false
  type = 7
  expr: Placement = MirrorClip_AS.Placement * v5_6_Master#Local_CS088.Placement * AttachmentOffset
FEATURE [Part::FeaturePython] Nut007  label="M4-Nut084"  # Fasteners workbench fastener (typed FeaturePython)
  AssemblyType = Asm4EE
  AttachedBy = Origin
  AttachedTo = MirrorClip_FS#Local_CS087
  AttachmentOffset = pos=(0,0,24) rot=(0,0,1;1.5708rad)
  Placement = pos=(-81.3173,-70.7107,-7) rot=(0,0,-1;0.785398rad)
  diameter = 6
  invert = false
  matchOuter = false
  offset = 0
  thread = false
  type = 7
  expr: Placement = MirrorClip_FS.Placement * v5_6_Master#Local_CS087.Placement * AttachmentOffset
FEATURE [Part::FeaturePython] Nut008  label="M4-Nut085"  # Fasteners workbench fastener (typed FeaturePython)
  AssemblyType = Asm4EE
  AttachedBy = Origin
  AttachedTo = MirrorClip_FS#Local_CS088
  AttachmentOffset = pos=(0,0,24) rot=(0,0,1;1.5708rad)
  Placement = pos=(-70.7107,-81.3173,-7) rot=(0,0,-1;0.785398rad)
  diameter = 6
  invert = false
  matchOuter = false
  offset = 0
  thread = false
  type = 7
  expr: Placement = MirrorClip_FS.Placement * v5_6_Master#Local_CS088.Placement * AttachmentOffset
FEATURE [App::Link] RockerKnob_AP
  AssemblyType = Asm4EE
  AttachedBy = #Local_CS235
  AttachedTo = Rocker_P#Local_CS028
  LinkPlacement = pos=(133,113,-65.2) rot=(-0.57735,-0.57735,-0.57735;4.18879rad)
  LinkedObject = -> <external v5.6_Master.FCStd>#Body022032
  Placement = pos=(133,113,-65.2) rot=(-0.57735,-0.57735,-0.57735;4.18879rad)
  expr: Placement = Rocker_P.Placement * v5_6_Master#Local_CS028.Placement * AttachmentOffset * v5_6_Master#Local_CS235.Placement ^ -1
FEATURE [App::Link] RockerKnob_FP
  AssemblyType = Asm4EE
  AttachedBy = #Local_CS235
  AttachedTo = Rocker_P#Local_CS030
  LinkPlacement = pos=(133,-113,-65.2) rot=(-0.57735,-0.57735,-0.57735;4.18879rad)
  LinkedObject = -> <external v5.6_Master.FCStd>#Body022032
  Placement = pos=(133,-113,-65.2) rot=(-0.57735,-0.57735,-0.57735;4.18879rad)
  expr: Placement = Rocker_P.Placement * v5_6_Master#Local_CS030.Placement * AttachmentOffset * v5_6_Master#Local_CS235.Placement ^ -1
FEATURE [App::Link] RockerKnob_AS
  AssemblyType = Asm4EE
  AttachedBy = #Local_CS235
  AttachedTo = Rocker_S#Local_CS024
  LinkPlacement = pos=(-133,113,-65.2) rot=(-0.57735,-0.57735,0.57735;2.0944rad)
  LinkedObject = -> <external v5.6_Master.FCStd>#Body022032
  Placement = pos=(-133,113,-65.2) rot=(-0.57735,-0.57735,0.57735;2.0944rad)
  expr: Placement = Rocker_S.Placement * v5_6_Master#Local_CS024.Placement * AttachmentOffset * v5_6_Master#Local_CS235.Placement ^ -1
FEATURE [App::Link] RockerKnob_FS
  AssemblyType = Asm4EE
  AttachedBy = #Local_CS235
  AttachedTo = Rocker_S#Local_CS026
  LinkPlacement = pos=(-133,-113,-65.2) rot=(-0.57735,-0.57735,0.57735;2.0944rad)
  LinkedObject = -> <external v5.6_Master.FCStd>#Body022032
  Placement = pos=(-133,-113,-65.2) rot=(-0.57735,-0.57735,0.57735;2.0944rad)
  expr: Placement = Rocker_S.Placement * v5_6_Master#Local_CS026.Placement * AttachmentOffset * v5_6_Master#Local_CS235.Placement ^ -1
FEATURE [App::Link] CollKnob_AP001  label="CollKnob_AP"
  AssemblyType = Asm4EE
  AttachedBy = #Local_CS234
  AttachedTo = UpperCell#Local_CS011
  AttachmentOffset = pos=(0,0,1.6) rot=(0,0,1;0rad)
  LinkPlacement = pos=(92,92,-29.4) rot=(0,0,-1;1.5708rad)
  LinkedObject = -> <external v5.6_Master.FCStd>#Body022030
  Placement = pos=(92,92,-29.4) rot=(0,0,-1;1.5708rad)
  expr: Placement = UpperCell.Placement * v5_6_Master#Local_CS011.Placement * AttachmentOffset * v5_6_Master#Local_CS234.Placement ^ -1
FEATURE [App::Link] CollKnob_AS001  label="CollKnob_AS"
  AssemblyType = Asm4EE
  AttachedBy = #Local_CS234
  AttachedTo = UpperCell#Local_CS010
  AttachmentOffset = pos=(0,0,1.6) rot=(0,0,1;0rad)
  LinkPlacement = pos=(-92,92,-29.4) rot=(0,0,-1;1.5708rad)
  LinkedObject = -> <external v5.6_Master.FCStd>#Body022030
  Placement = pos=(-92,92,-29.4) rot=(0,0,-1;1.5708rad)
  expr: Placement = UpperCell.Placement * v5_6_Master#Local_CS010.Placement * AttachmentOffset * v5_6_Master#Local_CS234.Placement ^ -1
FEATURE [App::Link] PoleBase_TNut_AS
  AssemblyType = Asm4EE
  AttachedBy = #Local_CS100
  AttachedTo = LowerCell#LCS_LowerCell_Pole_AS
  AttachmentOffset = pos=(0,0,10) rot=(0,0,1;1.5708rad)
  LinkPlacement = pos=(-113,113,-56.4) rot=(0,0,1;4.71239rad)
  LinkedObject = -> <external v5.6_Master.FCStd>#Body039
  Placement = pos=(-113,113,-56.4) rot=(0,0,1;4.71239rad)
  expr: Placement = LowerCell.Placement * v5_6_Master#LCS_LowerCell_Pole_AS.Placement * AttachmentOffset * v5_6_Master#Local_CS100.Placement ^ -1
FEATURE [App::Link] PoleBase_TNut_FS
  AssemblyType = Asm4EE
  AttachedBy = #Local_CS100
  AttachedTo = LowerCell#LCS_LowerCell_Pole_FS
  AttachmentOffset = pos=(0,0,0) rot=(0,0,1;1.5708rad)
  LinkPlacement = pos=(-113,-113,-56.4) rot=(0,0,1;4.71239rad)
  LinkedObject = -> <external v5.6_Master.FCStd>#Body039
  Placement = pos=(-113,-113,-56.4) rot=(0,0,1;4.71239rad)
  expr: Placement = LowerCell.Placement * v5_6_Master#LCS_LowerCell_Pole_FS.Placement * AttachmentOffset * v5_6_Master#Local_CS100.Placement ^ -1
FEATURE [App::Part] Model  label="Primary"
  Configuration = 0
  Group = -> [LCS_Origin,Constraints,Variables,PrimaryMirror,UpperCell,LowerPad_A,LowerPad_FP,LowerPad_FS,LowerCell,Rocker_P,Rocker_S,LCFrame_Bracket_AP,LCFrame_Bracket_AS,CollSpring_F,CollSpring_AP,CollSpring_AS,MirrorClip_AP,MirrorClip_FP,MirrorClip_AS,MirrorClip_FS,Rocker_P_TNut_A,Rocker_P_TNut_F,Rocker_S_TNut_A,Rocker_S_TNut_F,LCBracket_AP_TNut_P,LCBracket_AP_TNut_A,LCBracket_AS_TNut_S,LCBracket_AS_TNut_A,+55 more]
  Origin = -> Origin
  Type = Assembly4 Model

RESOLVED EXTERNAL PARTS (link-assembly join: the EXTERNAL_REF files above that resolve inside this repo's crawl, each included once):
---- part v5.6_Master.FCStd = doc fcstd_204eddf974d0 (447149 chars; too large to inline — full recipe in that document) ----
